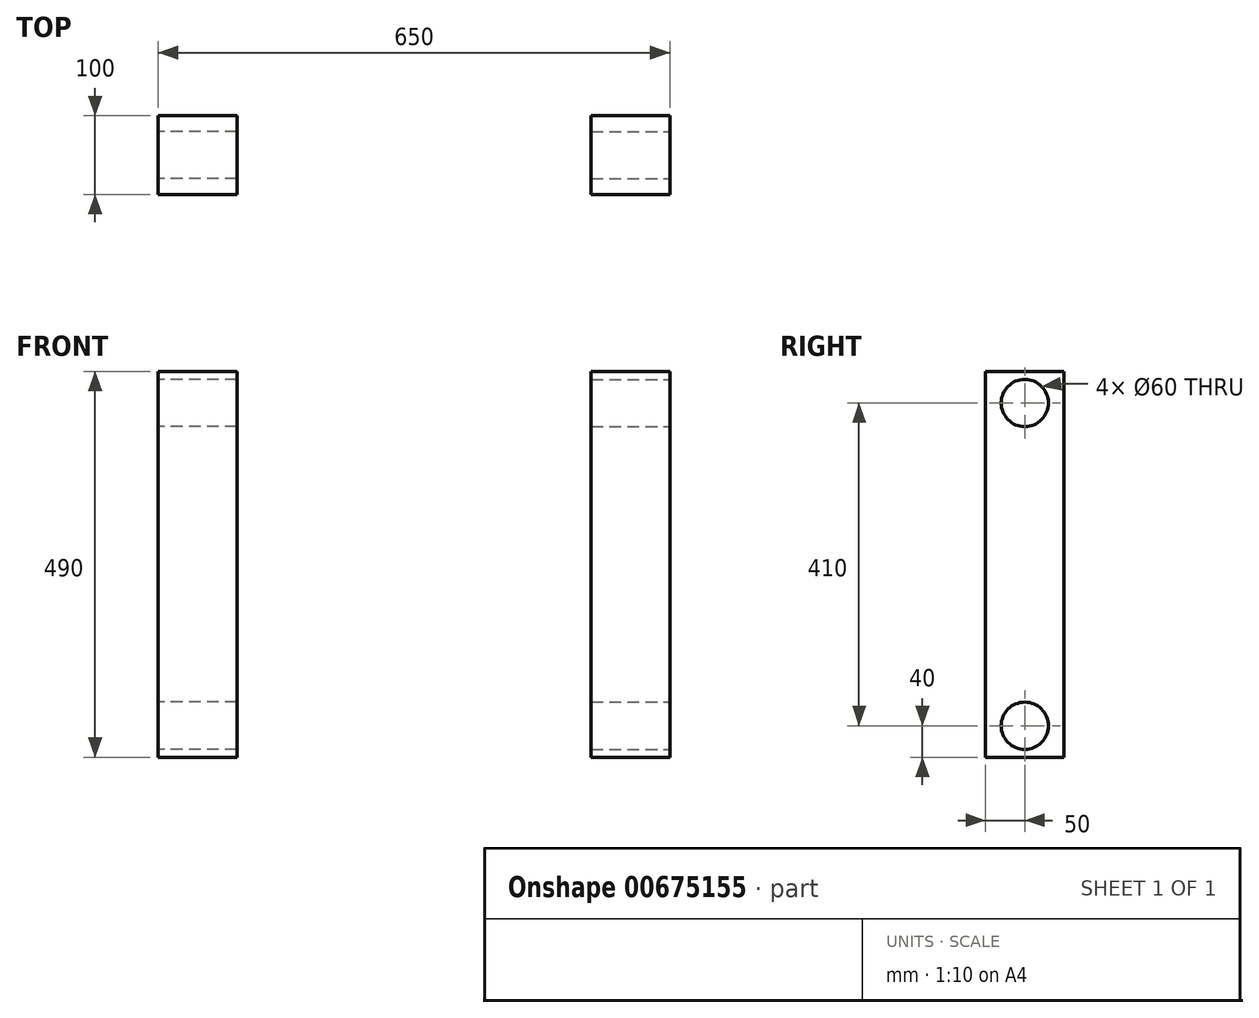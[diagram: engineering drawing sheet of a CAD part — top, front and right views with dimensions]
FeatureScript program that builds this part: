
annotation { "Feature Type Name" : "Feature", "Feature Type Description" : "" }
export const myFeature = defineFeature(function(context is Context, id is Id, definition is map)
    precondition{}
    {
        {
            var Q0;
            Q0=qCreatedBy(makeId("Top.planeOp"),FACE);
            var sketch = newSketch(context, id + "F0", { "sketchPlane" : qUnion([Q0])});
            skLineSegment(sketch, "E0.bottom", {"start": v(-325, 50) * mm, "end": v(-225, 50) * mm});
            skLineSegment(sketch, "E0.top", {"start": v(-325, -50) * mm, "end": v(-225, -50) * mm});
            skLineSegment(sketch, "E0.left", {"start": v(-325, 50) * mm, "end": v(-325, -50) * mm});
            skLineSegment(sketch, "E0.right", {"start": v(-225, 50) * mm, "end": v(-225, -50) * mm});
            skLineSegment(sketch, "E1.bottom", {"start": v(225, 50) * mm, "end": v(325, 50) * mm});
            skLineSegment(sketch, "E1.top", {"start": v(225, -50) * mm, "end": v(325, -50) * mm});
            skLineSegment(sketch, "E1.left", {"start": v(225, 50) * mm, "end": v(225, -50) * mm});
            skLineSegment(sketch, "E1.right", {"start": v(325, 50) * mm, "end": v(325, -50) * mm});
            skSolve(sketch);
        }
        {
            var Q0;
            Q0=makeQuery(id+"F0.imprint","IMPRINT",FACE,{"disambiguationData":[TD([[makeQuery(id+"F0.imprint","IMPRINT",EDGE,{"derivedFrom":sQuery(id+"F0.wireOp",EDGE,"E0.bottom")}),-1.0]])]});
            var Q1;
            Q1=makeQuery(id+"F0.imprint","IMPRINT",FACE,{"disambiguationData":[TD([[makeQuery(id+"F0.imprint","IMPRINT",EDGE,{"derivedFrom":sQuery(id+"F0.wireOp",EDGE,"E1.bottom")}),-1.0]])]});
            extrude(context, id + "F1", {"entities" : qUnion([Q0, Q1]), "depth" : 490 * mm, "offsetDistance" : 25 * mm});
        }
        {
            var Q0;
            Q0=makeQuery(id+"F1.opExtrude","SWEPT_FACE",FACE,{"disambiguationData":[OSD([sQuery(id+"F0.wireOp",EDGE,"E0.left")])]});
            var sketch = newSketch(context, id + "F2", { "sketchPlane" : qUnion([Q0])});
            skCircle(sketch, "E2", {"center": v(0, 450) * mm, "radius": 30 * mm});
            skSolve(sketch);
        }
        {
            var Q0;
            Q0 = qSketchRegion(id + "F2", true);
            extrude(context, id + "F3", {"entities" : qUnion([Q0]), "operationType" : NewBodyOperationType.REMOVE, "oppositeDirection" : true, "depth" : 100 * mm, "offsetDistance" : 25 * mm});
        }
        {
            var Q0;
            Q0=makeQuery(id+"F1.opExtrude","SWEPT_FACE",FACE,{"disambiguationData":[OSD([sQuery(id+"F0.wireOp",EDGE,"E1.right")])]});
            var sketch = newSketch(context, id + "F4", { "sketchPlane" : qUnion([Q0])});
            skCircle(sketch, "E3", {"center": v(0, 450) * mm, "radius": 30 * mm});
            skSolve(sketch);
        }
        {
            var Q0;
            Q0=makeQuery(id+"F4.imprint","IMPRINT",FACE,{"disambiguationData":[TD([[makeQuery(id+"F4.imprint","IMPRINT",EDGE,{"derivedFrom":sQuery(id+"F4.wireOp",EDGE,"E3")}),1.0]])]});
            extrude(context, id + "F5", {"entities" : qUnion([Q0]), "operationType" : NewBodyOperationType.REMOVE, "oppositeDirection" : true, "depth" : 100 * mm, "offsetDistance" : 25 * mm});
        }
        {
            var Q0;
            Q0=makeQuery(id+"F1.opExtrude","SWEPT_FACE",FACE,{"disambiguationData":[OSD([sQuery(id+"F0.wireOp",EDGE,"E1.right")])]});
            var sketch = newSketch(context, id + "F6", { "sketchPlane" : qUnion([Q0])});
            skCircle(sketch, "E4", {"center": v(0, 40) * mm, "radius": 30 * mm});
            skSolve(sketch);
        }
        {
            var Q0;
            Q0=makeQuery(id+"F6.imprint","IMPRINT",FACE,{"disambiguationData":[TD([[makeQuery(id+"F6.imprint","IMPRINT",EDGE,{"derivedFrom":sQuery(id+"F6.wireOp",EDGE,"E4")}),1.0]])]});
            extrude(context, id + "F7", {"entities" : qUnion([Q0]), "operationType" : NewBodyOperationType.REMOVE, "oppositeDirection" : true, "depth" : 100 * mm, "offsetDistance" : 25 * mm});
        }
        {
            var Q0;
            Q0=makeQuery(id+"F1.opExtrude","SWEPT_FACE",FACE,{"disambiguationData":[OSD([sQuery(id+"F0.wireOp",EDGE,"E0.left")])]});
            var sketch = newSketch(context, id + "F8", { "sketchPlane" : qUnion([Q0])});
            skCircle(sketch, "E5", {"center": v(0, 40) * mm, "radius": 30 * mm});
            skSolve(sketch);
        }
        {
            var Q0;
            Q0=makeQuery(id+"F8.imprint","IMPRINT",FACE,{"disambiguationData":[TD([[makeQuery(id+"F8.imprint","IMPRINT",EDGE,{"derivedFrom":sQuery(id+"F8.wireOp",EDGE,"E5")}),1.0]])]});
            extrude(context, id + "F9", {"entities" : qUnion([Q0]), "operationType" : NewBodyOperationType.REMOVE, "oppositeDirection" : true, "depth" : 100 * mm, "offsetDistance" : 25 * mm});
        }
    });
